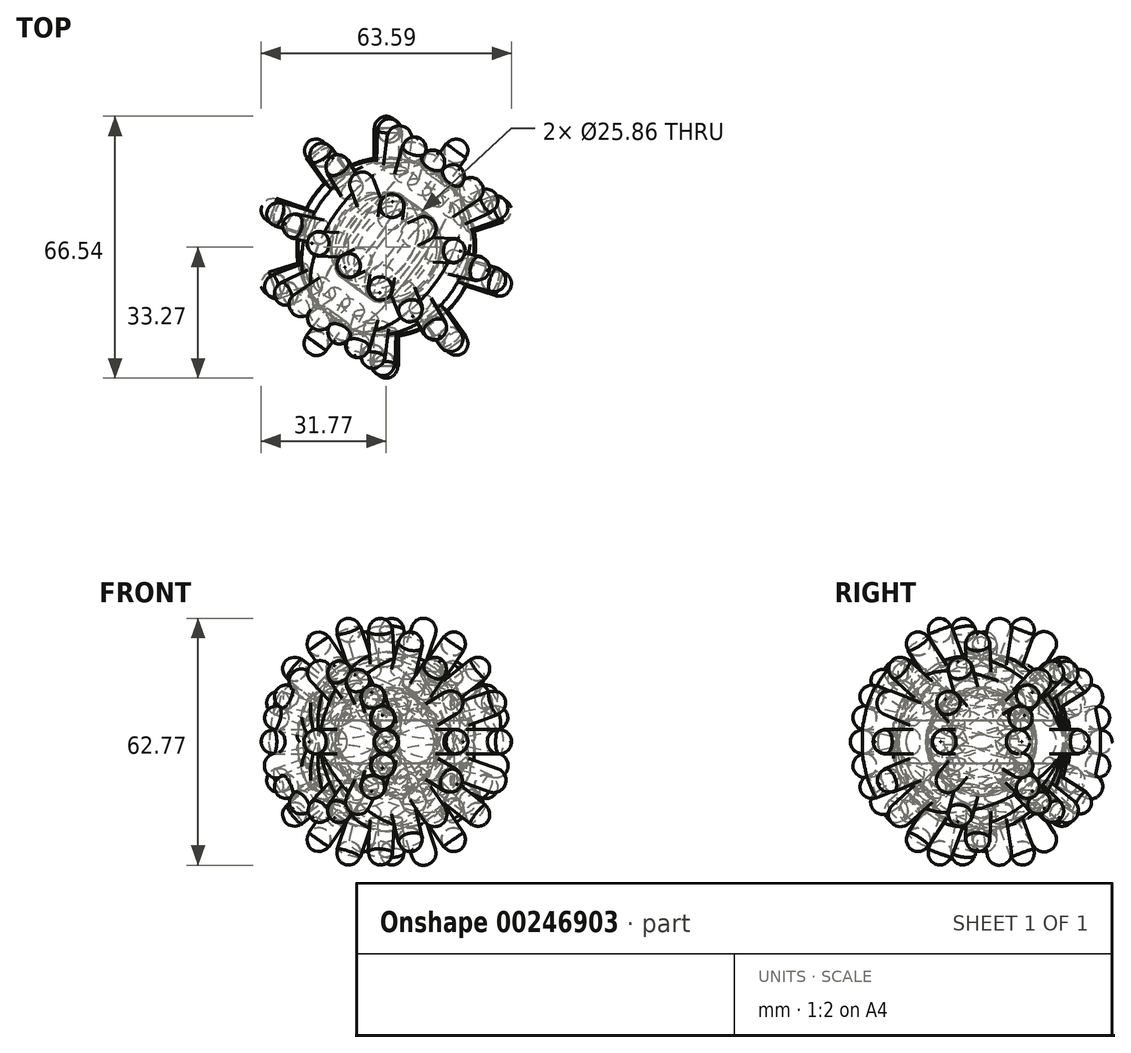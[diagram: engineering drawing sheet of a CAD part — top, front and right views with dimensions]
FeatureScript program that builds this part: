
annotation { "Feature Type Name" : "Feature", "Feature Type Description" : "" }
export const myFeature = defineFeature(function(context is Context, id is Id, definition is map)
    precondition{}
    {
        {
            var Q0;
            Q0=qCreatedBy(makeId("Top.planeOp"),FACE);
            var sketch = newSketch(context, id + "F0", { "sketchPlane" : qUnion([Q0])});
            skCircle(sketch, "E0", {"center": v(0, 0) * mm, "radius": 12.93 * mm});
            skCircle(sketch, "E1", {"center": v(0, 0) * mm, "radius": 22.36 * mm});
            skSolve(sketch);
        }
        {
            var Q0;
            Q0=makeQuery(id+"F0.imprint","IMPRINT",FACE,{"disambiguationData":[TD([[makeQuery(id+"F0.imprint","IMPRINT",EDGE,{"derivedFrom":sQuery(id+"F0.wireOp",EDGE,"E0")}),-1.0]])]});
            extrude(context, id + "F1", {"entities" : qUnion([Q0]), "oppositeDirection" : true, "depth" : 10.92 * mm});
        }
        {
            var Q0;
            Q0=makeQuery(id+"F1.opExtrude","CAP_EDGE",EDGE,{"disambiguationData":[OSD([sQuery(id+"F0.wireOp",EDGE,"E1")])],"isStart":true});
            var Q1;
            Q1=makeQuery(id+"F1.opExtrude","CAP_EDGE",EDGE,{"disambiguationData":[OSD([sQuery(id+"F0.wireOp",EDGE,"E1")])],"isStart":false});
            fillet(context, id + "F2", {"entities" : qUnion([Q0, Q1]), "radius" : 1.27 * mm, "tangentPropagation" : true, "allowEdgeOverflow" : false});
        }
        {
            var Q0;
            Q0=qCreatedBy(makeId("Front.planeOp"),FACE);
            var sketch = newSketch(context, id + "F3", { "sketchPlane" : qUnion([Q0])});
            skCircle(sketch, "E2", {"center": v(0, -5.46) * mm, "radius": 3.12 * mm});
            skSolve(sketch);
        }
        {
            var Q0;
            Q0=makeQuery(id+"F3.imprint","IMPRINT",FACE,{"disambiguationData":[TD([[makeQuery(id+"F3.imprint","IMPRINT",EDGE,{"derivedFrom":sQuery(id+"F3.wireOp",EDGE,"E2")}),1.0]])]});
            extrude(context, id + "F4", {"entities" : qUnion([Q0]), "oppositeDirection" : true, "depth" : 33.27 * mm, "hasSecondDirection" : true, "secondDirectionOppositeDirection" : true, "secondDirectionDepth" : 21.34 * mm});
        }
        {
            var Q0;
            Q0=makeQuery(id+"F4.opExtrude","CAP_EDGE",EDGE,{"disambiguationData":[OSD([sQuery(id+"F3.wireOp",EDGE,"E2")])],"isStart":false});
            fillet(context, id + "F5", {"entities" : qUnion([Q0]), "radius" : 3.05 * mm, "allowEdgeOverflow" : false});
        }
        {
            var Q0;
            Q0=makeQuery(id+"F4.opExtrude","SWEPT_BODY",BODY,{"disambiguationData":[OSD([sQuery(id+"F3.wireOp",EDGE,"E2")])]});
            var Q1;
            Q1=makeQuery(id+"F1.opExtrude","SWEPT_FACE",FACE,{"disambiguationData":[OSD([sQuery(id+"F0.wireOp",EDGE,"E1")])]});
            circularPattern(context, id + "F6", {"entities" : qUnion([Q0]), "axis" : qUnion([Q1]), "angle" : 360 * degree, "instanceCount" : 10, "equalSpace" : true});
        }
        {
            var Q0;
            Q0=makeQuery(id+"F1.opExtrude","SWEPT_BODY",BODY,{"disambiguationData":[OSD([sQuery(id+"F0.wireOp",EDGE,"E0"),sQuery(id+"F0.wireOp",EDGE,"E1")])]});
            var Q1;
            Q1=makeQuery(id+"F6.opPattern","COPY",BODY,{"derivedFrom":makeQuery(id+"F4.opExtrude","SWEPT_BODY",BODY,{"disambiguationData":[OSD([sQuery(id+"F3.wireOp",EDGE,"E2")])]}),"instanceName":"8"});
            var Q2;
            Q2=makeQuery(id+"F6.opPattern","COPY",BODY,{"derivedFrom":makeQuery(id+"F4.opExtrude","SWEPT_BODY",BODY,{"disambiguationData":[OSD([sQuery(id+"F3.wireOp",EDGE,"E2")])]}),"instanceName":"7"});
            var Q3;
            Q3=makeQuery(id+"F6.opPattern","COPY",BODY,{"derivedFrom":makeQuery(id+"F4.opExtrude","SWEPT_BODY",BODY,{"disambiguationData":[OSD([sQuery(id+"F3.wireOp",EDGE,"E2")])]}),"instanceName":"6"});
            var Q4;
            Q4=makeQuery(id+"F6.opPattern","COPY",BODY,{"derivedFrom":makeQuery(id+"F4.opExtrude","SWEPT_BODY",BODY,{"disambiguationData":[OSD([sQuery(id+"F3.wireOp",EDGE,"E2")])]}),"instanceName":"5"});
            var Q5;
            Q5=makeQuery(id+"F6.opPattern","COPY",BODY,{"derivedFrom":makeQuery(id+"F4.opExtrude","SWEPT_BODY",BODY,{"disambiguationData":[OSD([sQuery(id+"F3.wireOp",EDGE,"E2")])]}),"instanceName":"4"});
            var Q6;
            Q6=makeQuery(id+"F6.opPattern","COPY",BODY,{"derivedFrom":makeQuery(id+"F4.opExtrude","SWEPT_BODY",BODY,{"disambiguationData":[OSD([sQuery(id+"F3.wireOp",EDGE,"E2")])]}),"instanceName":"3"});
            var Q7;
            Q7=makeQuery(id+"F6.opPattern","COPY",BODY,{"derivedFrom":makeQuery(id+"F4.opExtrude","SWEPT_BODY",BODY,{"disambiguationData":[OSD([sQuery(id+"F3.wireOp",EDGE,"E2")])]}),"instanceName":"2"});
            var Q8;
            Q8=makeQuery(id+"F6.opPattern","COPY",BODY,{"derivedFrom":makeQuery(id+"F4.opExtrude","SWEPT_BODY",BODY,{"disambiguationData":[OSD([sQuery(id+"F3.wireOp",EDGE,"E2")])]}),"instanceName":"1"});
            var Q9;
            Q9=makeQuery(id+"F4.opExtrude","SWEPT_BODY",BODY,{"disambiguationData":[OSD([sQuery(id+"F3.wireOp",EDGE,"E2")])]});
            var Q10;
            Q10=makeQuery(id+"F6.opPattern","COPY",FACE,{"derivedFrom":makeQuery(id+"F4.opExtrude","SWEPT_FACE",FACE,{"disambiguationData":[OSD([sQuery(id+"F3.wireOp",EDGE,"E2")])]}),"instanceName":"9"});
            circularPattern(context, id + "F7", {"entities" : qUnion([Q0, Q1, Q2, Q3, Q4, Q5, Q6, Q7, Q8, Q9]), "axis" : qUnion([Q10]), "angle" : 20 * degree, "instanceCount" : 10});
        }
    });
